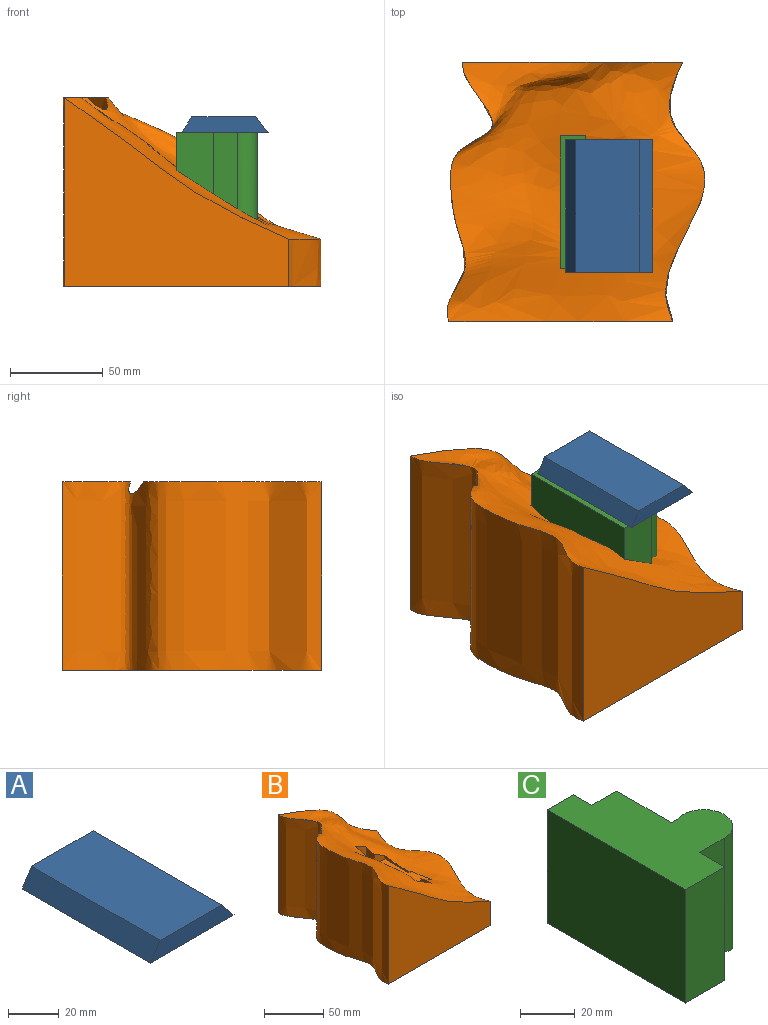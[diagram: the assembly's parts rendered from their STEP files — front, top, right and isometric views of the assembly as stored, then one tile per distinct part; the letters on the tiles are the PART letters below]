
ASSEMBLY  parts=3 mates=2
PART A: 6 faces, bbox 46.6x71.6x8.3 mm
  f0: plane 46.6x8.29mm, normal (0,-1,0), area 335.2mm2, adj f1,f2,f3,f4
  f1: plane 71.62x8.29mm, normal (-0.84,0,0.55), area 709.4mm2, adj f0,f2,f3,f5
  f2: plane 71.62x34.23mm, normal (0,0,1), area 2451.6mm2, adj f0,f1,f4,f5
  f3: plane 71.62x46.6mm, normal (0,0,-1), area 3337.5mm2, adj f0,f1,f4,f5
  f4: plane 71.62x8.29mm, normal (0.77,0,0.64), area 775.1mm2, adj f0,f2,f3,f5
  f5: plane 46.6x8.29mm, normal (0,1,0), area 335.2mm2, adj f1,f2,f3,f4
PART B: 16 faces, bbox 143.1x144.9x104.1 mm
  f0: bspline ~139.86x138.92mm, area 18105.6mm2, adj f1,f2,f3,f4,f6,f7,f8,f9
  f1: extruded ~139.86x101.6mm, area 15943.3mm2, adj f0,f2,f4,f5
  f2: plane 122.05x102.71mm, normal (0,-1,0), area 7220.6mm2, adj f0,f1,f3,f5
  f3: extruded ~139.86x25.4mm, area 3847.9mm2, adj f0,f2,f4,f5
  f4: plane 119.86x102.6mm, normal (0,1,0), area 8200.4mm2, adj f0,f1,f3,f5
  f5: plane 142.43x140.62mm, normal (0,0,-1), area 16521.8mm2, adj f1,f2,f3,f4
  f6: plane 71.62x23.46mm, normal (1,0,0), area 1403.9mm2, adj f0,f7,f14,f15
  f7: plane 22.56x21.01mm, normal (0,1,0), area 311.9mm2, adj f0,f6,f8,f15
  f8: plane 15.69x11.55mm, normal (-1,0,0), area 110.4mm2, adj f0,f7,f9,f15
  f9: plane 13.24x7.5mm, normal (0,1,0), area 43.1mm2, adj f0,f8,f15
  f10: plane 3.2x1.31mm, normal (0,-1,0), area 2mm2, adj f0,f11,f15
  f11: plane 28.38x4.13mm, normal (-1,0,0), area 53.2mm2, adj f0,f10,f12,f15
  f12: plane 13.19x11.14mm, normal (0,-1,0), area 95mm2, adj f0,f11,f13,f15
  f13: plane 14.47x9.79mm, normal (-1,0,0), area 118.3mm2, adj f0,f12,f14,f15
  f14: plane 22.12x13.8mm, normal (0,-1,0), area 241.7mm2, adj f0,f6,f13,f15
  f15: plane 72.54x33.97mm, normal (0,0,1), area 1782.3mm2, adj f0,f6,f7,f8,f9,f10,f11,f12
PART C: 13 faces, bbox 92.6x71.6x66 mm
  f0: plane 71.62x33.05mm, normal (0,0,-1), area 1782.3mm2, adj f1,f3,f4,f5,f6,f7,f8,f9
  f1: plane 50.8x12.78mm, normal (0,-1,0), area 649.1mm2, adj f0,f2,f10,f11
  f2: cylinder r=10.6mm len=55.94mm, axis (0,0,-1), area 1995.6mm2, adj f1,f3,f11,f12
  f3: plane 50.8x3.17mm, normal (0,1,0), area 161.2mm2, adj f0,f2,f4,f11
  f4: plane 50.8x28.38mm, normal (1,0,0), area 1441.6mm2, adj f0,f3,f5,f11
  f5: plane 50.8x12.84mm, normal (0,1,0), area 652.1mm2, adj f0,f4,f6,f11
  f6: plane 50.8x9.46mm, normal (1,0,0), area 480.5mm2, adj f0,f5,f7,f11
  f7: plane 50.8x13.51mm, normal (0,1,0), area 686.5mm2, adj f0,f6,f8,f11
  f8: plane 71.62x50.8mm, normal (-1,0,0), area 3638.3mm2, adj f0,f7,f9,f11
  f9: plane 50.8x20.27mm, normal (0,-1,0), area 1029.7mm2, adj f0,f8,f10,f11
  f10: plane 50.8x13.18mm, normal (1,0,0), area 669.3mm2, adj f0,f1,f9,f11
  f11: plane 71.62x43.65mm, normal (0,0,1), area 2001.7mm2, adj f1,f2,f3,f4,f5,f6,f7,f8
  f12: bspline ~92.58x52.45mm, area 237.1mm2, adj f0,f2
PLACE A t=(0.99,-16.42,54.64)mm
PLACE B t=(5.41,-18.63,-28.44)mm
PLACE C t=(5.41,-18.96,-36.8)mm
MATE fastened A.f3 <-> C.f11  axis (0,0,-1) through (-2.53,-14.39,54.64)mm
MATE fastened C.f8 <-> B.f6  axis (-1,0,0) through (-28.88,-12.37,29.24)mm
